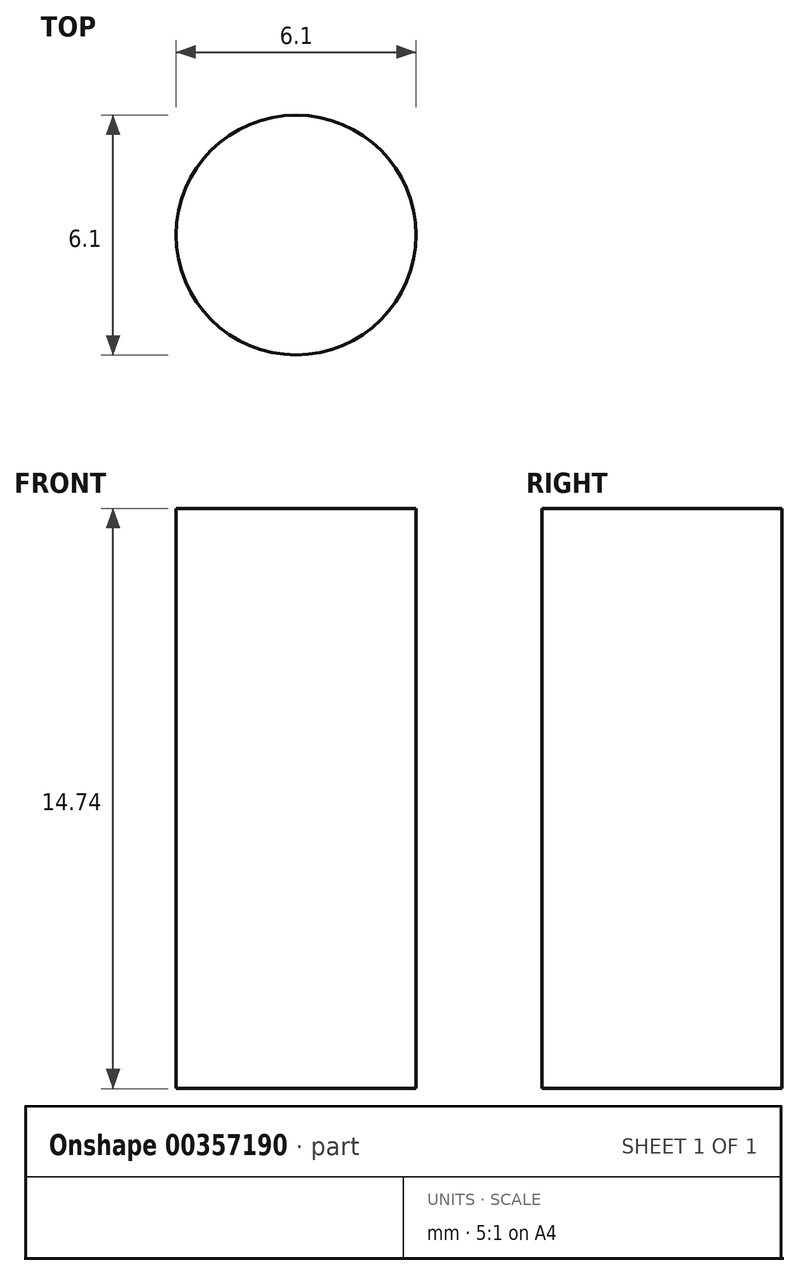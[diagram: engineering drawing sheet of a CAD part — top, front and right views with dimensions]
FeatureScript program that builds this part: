
annotation { "Feature Type Name" : "Feature", "Feature Type Description" : "" }
export const myFeature = defineFeature(function(context is Context, id is Id, definition is map)
    precondition{}
    {
        {
            var Q0;
            Q0=qCreatedBy(makeId("Top.planeOp"),FACE);
            var sketch = newSketch(context, id + "F0", { "sketchPlane" : qUnion([Q0])});
            skCircle(sketch, "E0", {"center": v(0, 0) * mm, "radius": 3.05 * mm});
            skSolve(sketch);
        }
        {
            var Q0;
            Q0 = qSketchRegion(id + "F0", true);
            extrude(context, id + "F1", {"entities" : qUnion([Q0]), "endBound" : BoundingType.SYMMETRIC, "depth" : 14.73 * mm});
        }
    });
